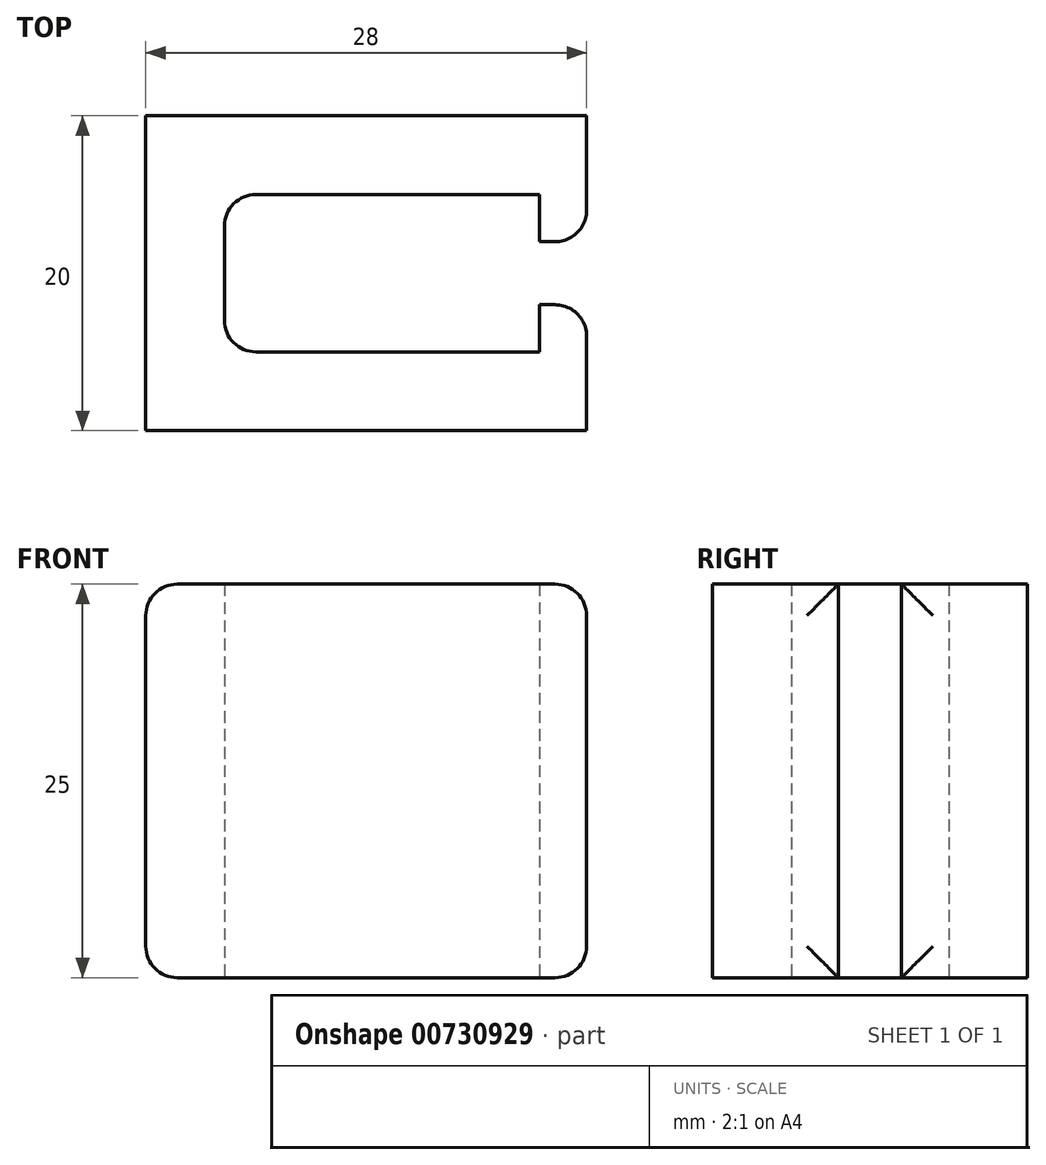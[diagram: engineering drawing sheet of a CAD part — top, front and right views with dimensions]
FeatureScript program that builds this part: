
annotation { "Feature Type Name" : "Feature", "Feature Type Description" : "" }
export const myFeature = defineFeature(function(context is Context, id is Id, definition is map)
    precondition{}
    {
        {
            var Q0;
            Q0=qCreatedBy(makeId("Top.planeOp"),FACE);
            var sketch = newSketch(context, id + "F0", { "sketchPlane" : qUnion([Q0])});
            skLineSegment(sketch, "E0", {"start": v(23, 2) * mm, "end": v(23, 10) * mm});
            skLineSegment(sketch, "E1", {"start": v(23, 10) * mm, "end": v(-5, 10) * mm});
            skLineSegment(sketch, "E2", {"start": v(-5, 10) * mm, "end": v(-5, 0) * mm});
            skLineSegment(sketch, "E3", {"start": v(-5, 0) * mm, "end": v(0, 0) * mm});
            skLineSegment(sketch, "E4", {"start": v(0, 0) * mm, "end": v(0, 5) * mm});
            skLineSegment(sketch, "E5", {"start": v(0, 5) * mm, "end": v(20, 5) * mm});
            skLineSegment(sketch, "E6", {"start": v(20, 5) * mm, "end": v(20, 2) * mm});
            skLineSegment(sketch, "E7", {"start": v(20, 2) * mm, "end": v(23, 2) * mm});
            skSolve(sketch);
        }
        {
            var Q0;
            Q0 = qSketchRegion(id + "F0", true);
            extrude(context, id + "F1", {"entities" : qUnion([Q0]), "depth" : 25 * mm, "offsetDistance" : 25 * mm});
        }
        {
            var Q0;
            Q0=makeQuery(id+"F1.opExtrude","SWEPT_BODY",BODY,{"disambiguationData":[OSD([sQuery(id+"F0.wireOp",EDGE,"E0"),sQuery(id+"F0.wireOp",EDGE,"E1"),sQuery(id+"F0.wireOp",EDGE,"E2"),sQuery(id+"F0.wireOp",EDGE,"E3"),sQuery(id+"F0.wireOp",EDGE,"E4"),sQuery(id+"F0.wireOp",EDGE,"E5"),sQuery(id+"F0.wireOp",EDGE,"E6"),sQuery(id+"F0.wireOp",EDGE,"E7")])]});
            var Q1;
            Q1=qCreatedBy(makeId("Front.planeOp"),FACE);
            mirror(context, id + "F2", {"operationType" : NewBodyOperationType.ADD, "entities" : qUnion([Q0]), "mirrorPlane" : qUnion([Q1])});
        }
        {
            var Q0;
            Q0=makeQuery(id+"F1.opExtrude","SWEPT_EDGE",EDGE,{"disambiguationData":[OSD([sQuery(id+"F0.wireOp",EDGE,"E4"),sQuery(id+"F0.wireOp",EDGE,"E5")])]});
            var Q1;
            Q1=makeQuery(id+"F2.opPattern","COPY",EDGE,{"derivedFrom":makeQuery(id+"F1.opExtrude","SWEPT_EDGE",EDGE,{"disambiguationData":[OSD([sQuery(id+"F0.wireOp",EDGE,"E4"),sQuery(id+"F0.wireOp",EDGE,"E5")])]}),"instanceName":"1"});
            var Q2;
            Q2=makeQuery(id+"F1.opExtrude","SWEPT_EDGE",EDGE,{"disambiguationData":[OSD([sQuery(id+"F0.wireOp",EDGE,"E0"),sQuery(id+"F0.wireOp",EDGE,"E7")])]});
            var Q3;
            Q3=makeQuery(id+"F2.opPattern","COPY",EDGE,{"derivedFrom":makeQuery(id+"F1.opExtrude","SWEPT_EDGE",EDGE,{"disambiguationData":[OSD([sQuery(id+"F0.wireOp",EDGE,"E0"),sQuery(id+"F0.wireOp",EDGE,"E7")])]}),"instanceName":"1"});
            var Q4;
            {var subQ0=makeQuery(id+"F1.opExtrude","CAP_EDGE",EDGE,{"disambiguationData":[OSD([sQuery(id+"F0.wireOp",EDGE,"E2")])],"isStart":false});Q4=makeQuery(id+"F2.boolean.opBoolean","MERGE",EDGE,{"derivedFrom":[subQ0,makeQuery(id+"F2.opPattern","COPY",EDGE,{"derivedFrom":subQ0,"instanceName":"1"})]});}
            var Q5;
            {var subQ0=makeQuery(id+"F1.opExtrude","CAP_EDGE",EDGE,{"disambiguationData":[OSD([sQuery(id+"F0.wireOp",EDGE,"E2")])],"isStart":true});Q5=makeQuery(id+"F2.boolean.opBoolean","MERGE",EDGE,{"derivedFrom":[subQ0,makeQuery(id+"F2.opPattern","COPY",EDGE,{"derivedFrom":subQ0,"instanceName":"1"})]});}
            var Q6;
            Q6=makeQuery(id+"F1.opExtrude","CAP_EDGE",EDGE,{"disambiguationData":[OSD([sQuery(id+"F0.wireOp",EDGE,"E0")])],"isStart":false});
            var Q7;
            Q7=makeQuery(id+"F2.opPattern","COPY",EDGE,{"derivedFrom":makeQuery(id+"F1.opExtrude","CAP_EDGE",EDGE,{"disambiguationData":[OSD([sQuery(id+"F0.wireOp",EDGE,"E0")])],"isStart":false}),"instanceName":"1"});
            var Q8;
            Q8=makeQuery(id+"F2.opPattern","COPY",EDGE,{"derivedFrom":makeQuery(id+"F1.opExtrude","CAP_EDGE",EDGE,{"disambiguationData":[OSD([sQuery(id+"F0.wireOp",EDGE,"E0")])],"isStart":true}),"instanceName":"1"});
            var Q9;
            Q9=makeQuery(id+"F1.opExtrude","CAP_EDGE",EDGE,{"disambiguationData":[OSD([sQuery(id+"F0.wireOp",EDGE,"E0")])],"isStart":true});
            fillet(context, id + "F3", {"entities" : qUnion([Q0, Q1, Q2, Q3, Q4, Q5, Q6, Q7, Q8, Q9]), "radius" : 2 * mm, "tangentPropagation" : true, "allowEdgeOverflow" : false});
        }
    });
